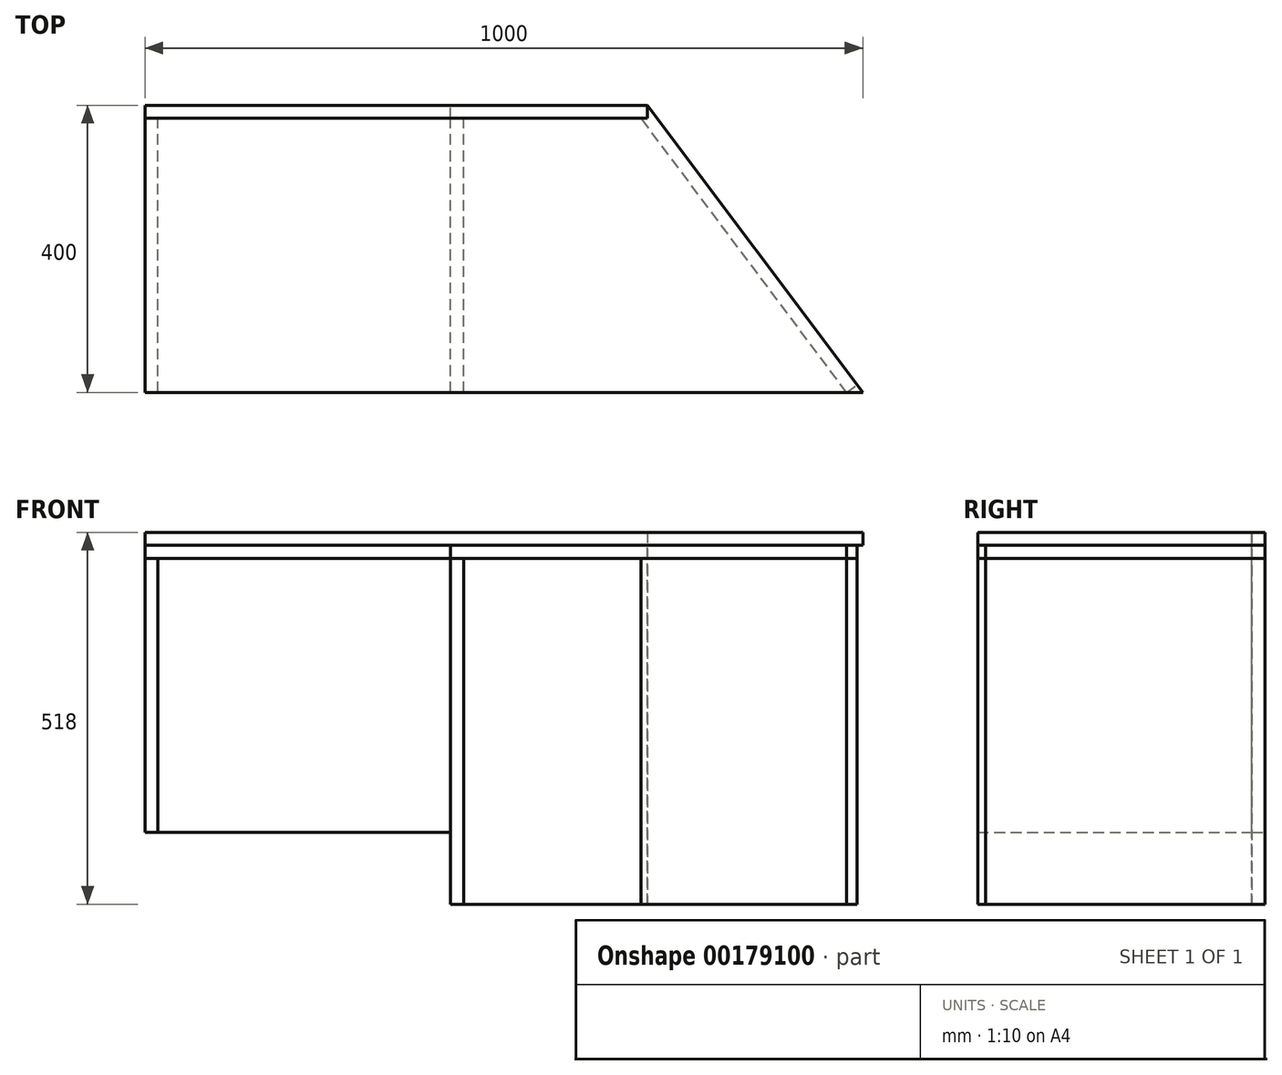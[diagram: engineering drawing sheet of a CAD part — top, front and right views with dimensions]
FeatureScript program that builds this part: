
annotation { "Feature Type Name" : "Feature", "Feature Type Description" : "" }
export const myFeature = defineFeature(function(context is Context, id is Id, definition is map)
    precondition{}
    {
        {
            var Q0;
            Q0=qCreatedBy(makeId("Top.planeOp"),FACE);
            var sketch = newSketch(context, id + "F0", { "sketchPlane" : qUnion([Q0])});
            skLineSegment(sketch, "E0", {"start": v(-528.36, -188.53) * mm, "end": v(-528.36, 211.47) * mm});
            skLineSegment(sketch, "E1", {"start": v(-528.36, 211.47) * mm, "end": v(171.64, 211.47) * mm});
            skLineSegment(sketch, "E2", {"start": v(171.64, 211.47) * mm, "end": v(471.64, -188.53) * mm});
            skLineSegment(sketch, "E3", {"start": v(471.64, -188.53) * mm, "end": v(-528.36, -188.53) * mm});
            skSolve(sketch);
        }
        {
            var Q0;
            Q0=makeQuery(id+"F0.imprint","IMPRINT",FACE,{"disambiguationData":[TD([[makeQuery(id+"F0.imprint","IMPRINT",EDGE,{"derivedFrom":sQuery(id+"F0.wireOp",EDGE,"E0")}),-1.0]])]});
            extrude(context, id + "F1", {"entities" : qUnion([Q0]), "depth" : 18 * mm});
        }
        {
            var Q0;
            Q0=makeQuery(id+"F1.opExtrude","CAP_FACE",FACE,{"disambiguationData":[OSD([sQuery(id+"F0.wireOp",EDGE,"E0"),sQuery(id+"F0.wireOp",EDGE,"E1"),sQuery(id+"F0.wireOp",EDGE,"E2"),sQuery(id+"F0.wireOp",EDGE,"E3")])],"isStart":true});
            var sketch = newSketch(context, id + "F2", { "sketchPlane" : qUnion([Q0])});
            skLineSegment(sketch, "E4.bottom", {"start": v(-528.36, 188.53) * mm, "end": v(-510.36, 188.53) * mm});
            skLineSegment(sketch, "E4.top", {"start": v(-528.36, -211.47) * mm, "end": v(-510.36, -211.47) * mm});
            skLineSegment(sketch, "E4.left", {"start": v(-528.36, 188.53) * mm, "end": v(-528.36, -211.47) * mm});
            skLineSegment(sketch, "E4.right", {"start": v(-510.36, 188.53) * mm, "end": v(-510.36, -211.47) * mm});
            skLineSegment(sketch, "E5.bottom", {"start": v(-102.81, 188.53) * mm, "end": v(-84.81, 188.53) * mm});
            skLineSegment(sketch, "E5.top", {"start": v(-102.81, -211.47) * mm, "end": v(-84.81, -211.47) * mm});
            skLineSegment(sketch, "E5.left", {"start": v(-102.81, 188.53) * mm, "end": v(-102.81, -211.47) * mm});
            skLineSegment(sketch, "E5.right", {"start": v(-84.81, 188.53) * mm, "end": v(-84.81, -211.47) * mm});
            skLineSegment(sketch, "E6", {"start": v(449.14, 188.53) * mm, "end": v(463.54, 177.73) * mm});
            skLineSegment(sketch, "E7", {"start": v(449.14, 188.53) * mm, "end": v(157.24, -200.67) * mm});
            skLineSegment(sketch, "E8", {"start": v(157.24, -200.67) * mm, "end": v(171.64, -211.47) * mm});
            skSolve(sketch);
        }
        {
            var Q0;
            Q0=makeQuery(id+"F2.imprint","IMPRINT",FACE,{"disambiguationData":[TD([[makeQuery(id+"F2.imprint","IMPRINT",EDGE,{"derivedFrom":sQuery(id+"F2.wireOp",EDGE,"E5.bottom")}),1.0]])]});
            var Q1;
            {var subQ0=sQuery(id+"F2.wireOp",EDGE,"E6");Q1=makeQuery(id+"F2.imprint","IMPRINT",FACE,{"disambiguationData":[TD([[makeQuery(id+"F2.imprint","IMPRINT",EDGE,{"derivedFrom":subQ0}),-1.0]])]});}
            extrude(context, id + "F3", {"entities" : qUnion([Q0, Q1]), "depth" : 500 * mm});
        }
        {
            var Q0;
            Q0=makeQuery(id+"F2.imprint","IMPRINT",FACE,{"disambiguationData":[TD([[makeQuery(id+"F2.imprint","IMPRINT",EDGE,{"derivedFrom":sQuery(id+"F2.wireOp",EDGE,"E4.bottom")}),1.0]])]});
            extrude(context, id + "F4", {"entities" : qUnion([Q0]), "depth" : 400 * mm});
        }
        {
            var Q0;
            Q0=makeQuery(id+"F2.imprint","IMPRINT",FACE,{"disambiguationData":[TD([[makeQuery(id+"F2.imprint","IMPRINT",EDGE,{"derivedFrom":sQuery(id+"F2.wireOp",EDGE,"E4.bottom")}),1.0]])]});
            var Q1;
            {var subQ0=sQuery(id+"F2.wireOp",EDGE,"E4.right");Q1=makeQuery(id+"F2.imprint","IMPRINT",FACE,{"disambiguationData":[TD([[makeQuery(id+"F2.imprint","IMPRINT",EDGE,{"derivedFrom":subQ0}),1.0]])]});}
            extrude(context, id + "F5", {"entities" : qUnion([Q0, Q1]), "depth" : 18 * mm});
        }
        {
            var Q0;
            Q0=makeQuery(id+"F2.imprint","IMPRINT",FACE,{"disambiguationData":[TD([[makeQuery(id+"F2.imprint","IMPRINT",EDGE,{"derivedFrom":sQuery(id+"F2.wireOp",EDGE,"E5.bottom")}),1.0]])]});
            var Q1;
            {var subQ2=sQuery(id+"F2.wireOp",EDGE,"E5.right");Q1=makeQuery(id+"F2.imprint","IMPRINT",FACE,{"disambiguationData":[TD([[makeQuery(id+"F2.imprint","IMPRINT",EDGE,{"derivedFrom":subQ2}),1.0]])]});}
            var Q2;
            {var subQ0=sQuery(id+"F2.wireOp",EDGE,"E6");Q2=makeQuery(id+"F2.imprint","IMPRINT",FACE,{"disambiguationData":[TD([[makeQuery(id+"F2.imprint","IMPRINT",EDGE,{"derivedFrom":subQ0}),-1.0]])]});}
            extrude(context, id + "F6", {"entities" : qUnion([Q0, Q1, Q2]), "depth" : 18 * mm});
        }
        {
            var Q0;
            Q0=makeQuery(id+"F1.opExtrude","SWEPT_FACE",FACE,{"disambiguationData":[OSD([sQuery(id+"F0.wireOp",EDGE,"E1")])]});
            var sketch = newSketch(context, id + "F7", { "sketchPlane" : qUnion([Q0])});
            skLineSegment(sketch, "E9", {"start": v(528.36, 18) * mm, "end": v(-171.64, 18) * mm});
            skLineSegment(sketch, "E10", {"start": v(-171.64, 18) * mm, "end": v(-171.64, -500) * mm});
            skLineSegment(sketch, "E11", {"start": v(-171.64, -500) * mm, "end": v(102.81, -500) * mm});
            skLineSegment(sketch, "E12", {"start": v(102.81, -500) * mm, "end": v(102.81, -400) * mm});
            skLineSegment(sketch, "E13", {"start": v(102.81, -400) * mm, "end": v(528.36, -400) * mm});
            skLineSegment(sketch, "E14", {"start": v(528.36, -400) * mm, "end": v(528.36, 18) * mm});
            skSolve(sketch);
        }
        {
            var Q0;
            {var subQ1=sQuery(id+"F7.wireOp",EDGE,"E11");Q0=makeQuery(id+"F7.imprint","IMPRINT",FACE,{"disambiguationData":[TD([[makeQuery(id+"F7.imprint","IMPRINT",EDGE,{"derivedFrom":subQ1}),1.0]])]});}
            var Q1;
            {var subQ0=sQuery(id+"F7.wireOp",EDGE,"E9");Q1=makeQuery(id+"F7.imprint","IMPRINT",FACE,{"disambiguationData":[TD([[makeQuery(id+"F7.imprint","IMPRINT",EDGE,{"derivedFrom":subQ0}),1.0]])]});}
            extrude(context, id + "F8", {"entities" : qUnion([Q0, Q1]), "oppositeDirection" : true, "depth" : 18 * mm});
        }
        {
            var Q0;
            Q0=makeQuery(id+"F8.opExtrude","SWEPT_BODY",BODY,{"disambiguationData":[OSD([sQuery(id+"F7.wireOp",EDGE,"E9"),sQuery(id+"F7.wireOp",EDGE,"E10"),sQuery(id+"F7.wireOp",EDGE,"E11"),sQuery(id+"F7.wireOp",EDGE,"E12"),sQuery(id+"F7.wireOp",EDGE,"E13"),sQuery(id+"F7.wireOp",EDGE,"E14")])]});
            var Q1;
            Q1=makeQuery(id+"F1.opExtrude","SWEPT_BODY",BODY,{"disambiguationData":[OSD([sQuery(id+"F0.wireOp",EDGE,"E0"),sQuery(id+"F0.wireOp",EDGE,"E1"),sQuery(id+"F0.wireOp",EDGE,"E2"),sQuery(id+"F0.wireOp",EDGE,"E3")])]});
            var Q2;
            Q2=makeQuery(id+"F3.opExtrude","SWEPT_BODY",BODY,{"disambiguationData":[OSD([sQuery(id+"F2.wireOp",EDGE,"E5.bottom"),sQuery(id+"F2.wireOp",EDGE,"E5.top"),sQuery(id+"F2.wireOp",EDGE,"E5.left"),sQuery(id+"F2.wireOp",EDGE,"E5.right")])]});
            var Q3;
            Q3=makeQuery(id+"F3.opExtrude","SWEPT_BODY",BODY,{"disambiguationData":[OSD([sQuery(id+"F0.wireOp",EDGE,"E2"),sQuery(id+"F2.wireOp",EDGE,"E6"),sQuery(id+"F2.wireOp",EDGE,"E7"),sQuery(id+"F2.wireOp",EDGE,"E8")])]});
            var Q4;
            Q4=makeQuery(id+"F4.opExtrude","SWEPT_BODY",BODY,{"disambiguationData":[OSD([sQuery(id+"F2.wireOp",EDGE,"E4.bottom"),sQuery(id+"F2.wireOp",EDGE,"E4.top"),sQuery(id+"F2.wireOp",EDGE,"E4.left"),sQuery(id+"F2.wireOp",EDGE,"E4.right")])]});
            var Q5;
            Q5=makeQuery(id+"F5.opExtrude","SWEPT_BODY",BODY,{"disambiguationData":[OSD([sQuery(id+"F0.wireOp",EDGE,"E1"),sQuery(id+"F0.wireOp",EDGE,"E3"),sQuery(id+"F2.wireOp",EDGE,"E4.bottom"),sQuery(id+"F2.wireOp",EDGE,"E4.top"),sQuery(id+"F2.wireOp",EDGE,"E4.left"),sQuery(id+"F2.wireOp",EDGE,"E5.left")])]});
            var Q6;
            Q6=makeQuery(id+"F6.opExtrude","SWEPT_BODY",BODY,{"disambiguationData":[OSD([sQuery(id+"F0.wireOp",EDGE,"E1"),sQuery(id+"F0.wireOp",EDGE,"E2"),sQuery(id+"F0.wireOp",EDGE,"E3"),sQuery(id+"F2.wireOp",EDGE,"E5.bottom"),sQuery(id+"F2.wireOp",EDGE,"E5.top"),sQuery(id+"F2.wireOp",EDGE,"E5.left"),sQuery(id+"F2.wireOp",EDGE,"E6")])]});
            booleanBodies(context, id + "F9", {"operationType" : BooleanOperationType.SUBTRACTION, "tools" : qUnion([Q0]), "targets" : qUnion([Q1, Q2, Q3, Q4, Q5, Q6]), "keepTools" : true});
        }
        {
            var Q0;
            Q0=makeQuery(id+"F5.opExtrude","SWEPT_BODY",BODY,{"disambiguationData":[OSD([sQuery(id+"F0.wireOp",EDGE,"E1"),sQuery(id+"F0.wireOp",EDGE,"E3"),sQuery(id+"F2.wireOp",EDGE,"E4.bottom"),sQuery(id+"F2.wireOp",EDGE,"E4.top"),sQuery(id+"F2.wireOp",EDGE,"E4.left"),sQuery(id+"F2.wireOp",EDGE,"E5.left")])]});
            var Q1;
            Q1=makeQuery(id+"F6.opExtrude","SWEPT_BODY",BODY,{"disambiguationData":[OSD([sQuery(id+"F0.wireOp",EDGE,"E1"),sQuery(id+"F0.wireOp",EDGE,"E2"),sQuery(id+"F0.wireOp",EDGE,"E3"),sQuery(id+"F2.wireOp",EDGE,"E5.bottom"),sQuery(id+"F2.wireOp",EDGE,"E5.top"),sQuery(id+"F2.wireOp",EDGE,"E5.left"),sQuery(id+"F2.wireOp",EDGE,"E6")])]});
            var Q2;
            Q2=makeQuery(id+"F3.opExtrude","SWEPT_BODY",BODY,{"disambiguationData":[OSD([sQuery(id+"F0.wireOp",EDGE,"E2"),sQuery(id+"F2.wireOp",EDGE,"E6"),sQuery(id+"F2.wireOp",EDGE,"E7"),sQuery(id+"F2.wireOp",EDGE,"E8")])]});
            var Q3;
            Q3=makeQuery(id+"F4.opExtrude","SWEPT_BODY",BODY,{"disambiguationData":[OSD([sQuery(id+"F2.wireOp",EDGE,"E4.bottom"),sQuery(id+"F2.wireOp",EDGE,"E4.top"),sQuery(id+"F2.wireOp",EDGE,"E4.left"),sQuery(id+"F2.wireOp",EDGE,"E4.right")])]});
            var Q4;
            Q4=makeQuery(id+"F3.opExtrude","SWEPT_BODY",BODY,{"disambiguationData":[OSD([sQuery(id+"F2.wireOp",EDGE,"E5.bottom"),sQuery(id+"F2.wireOp",EDGE,"E5.top"),sQuery(id+"F2.wireOp",EDGE,"E5.left"),sQuery(id+"F2.wireOp",EDGE,"E5.right")])]});
            booleanBodies(context, id + "F10", {"operationType" : BooleanOperationType.SUBTRACTION, "tools" : qUnion([Q0, Q1]), "targets" : qUnion([Q2, Q3, Q4]), "keepTools" : true});
        }
    });
